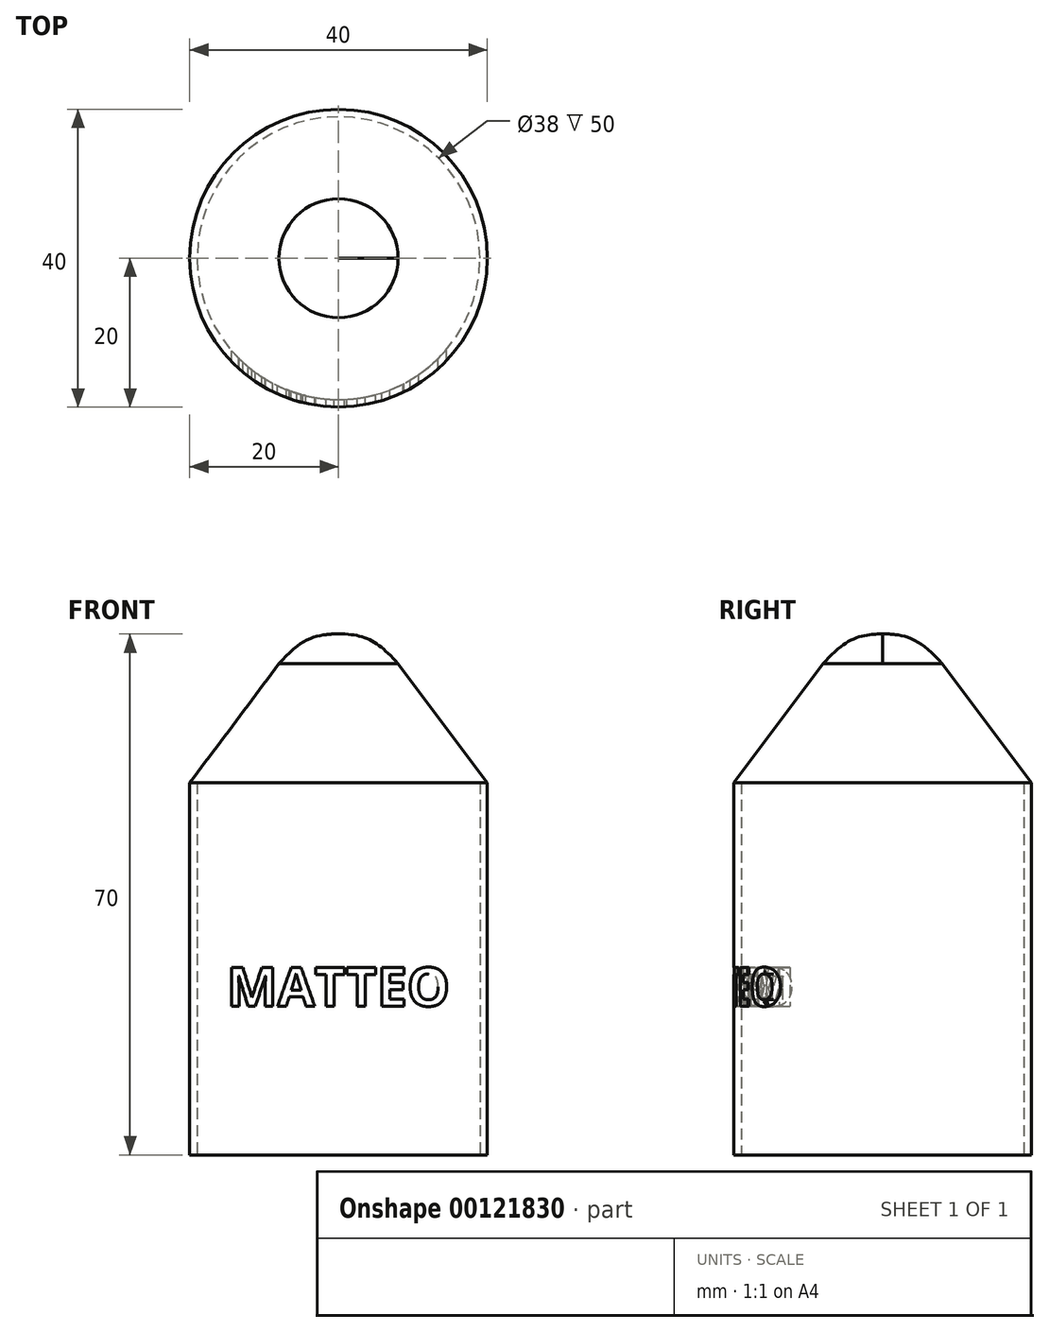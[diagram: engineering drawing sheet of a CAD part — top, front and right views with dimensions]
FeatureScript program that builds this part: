
annotation { "Feature Type Name" : "Feature", "Feature Type Description" : "" }
export const myFeature = defineFeature(function(context is Context, id is Id, definition is map)
    precondition{}
    {
        {
            var Q0;
            Q0=qCreatedBy(makeId("Top.planeOp"),FACE);
            var sketch = newSketch(context, id + "F0", { "sketchPlane" : qUnion([Q0])});
            skCircle(sketch, "E0", {"center": v(0, 0) * mm, "radius": 20 * mm});
            skCircle(sketch, "E1", {"center": v(0, 0) * mm, "radius": 19 * mm});
            skSolve(sketch);
        }
        {
            var Q0;
            Q0=qSketchRegion(id+"F0",true);
            var Q1;
            Q1=sQuery(id+"F0.wireOp",EDGE,"E0");
            var Q2;
            Q2=sQuery(id+"F0.wireOp",EDGE,"E1");
            extrude(context, id + "F1", {"entities" : qUnion([Q0]), "surfaceEntities" : qUnion([Q1, Q2]), "depth" : 50 * mm});
        }
        {
            var Q0;
            Q0=qCreatedBy(makeId("Front.planeOp"),FACE);
            var sketch = newSketch(context, id + "F2", { "sketchPlane" : qUnion([Q0])});
            skLineSegment(sketch, "E2", {"start": v(0, 50) * mm, "end": v(20, 50) * mm});
            skLineSegment(sketch, "E3", {"start": v(20, 50) * mm, "end": v(8, 66) * mm});
            skLineSegment(sketch, "E4", {"start": v(0, 50) * mm, "end": v(0, 70) * mm});
            skFitSpline(sketch, "E5", {"points": [v(8, 66) * mm, v(0, 70) * mm], "startDerivative": vector(-7.98, 9) * mm, "endDerivative": vector(-10.47, -0.14) * mm});
            skSolve(sketch);
        }
        {
            var Q0;
            Q0=makeQuery(id+"F2.imprint","IMPRINT",FACE,{"disambiguationData":[TD([[makeQuery(id+"F2.imprint","IMPRINT",EDGE,{"derivedFrom":sQuery(id+"F2.wireOp",EDGE,"E2")}),1.0]])]});
            var Q1;
            Q1=sQuery(id+"F2.wireOp",EDGE,"E4");
            revolve(context, id + "F3", {"operationType" : NewBodyOperationType.ADD, "entities" : qUnion([Q0]), "axis" : qUnion([Q1]), "revolveType" : RevolveType.FULL});
        }
        {
            var Q0;
            Q0=qCreatedBy(makeId("Front.planeOp"),FACE);
            var sketch = newSketch(context, id + "F4", { "sketchPlane" : qUnion([Q0])});
            skText(sketch, "E6", { "text": "MATTEO", "fontName": "OpenSans-Bold.ttf"});
            const initialGuessF4  = {"E6": [-0.015, 0.02, 1, 0, 0.0052]};
            skSetInitialGuess(sketch, initialGuessF4);
            skSolve(sketch);
        }
        {
            var Q0;
            Q0=qSketchRegion(id+"F4",true);
            extrude(context, id + "F5", {"entities" : qUnion([Q0]), "operationType" : NewBodyOperationType.REMOVE, "depth" : 53.9 * mm});
        }
    });
